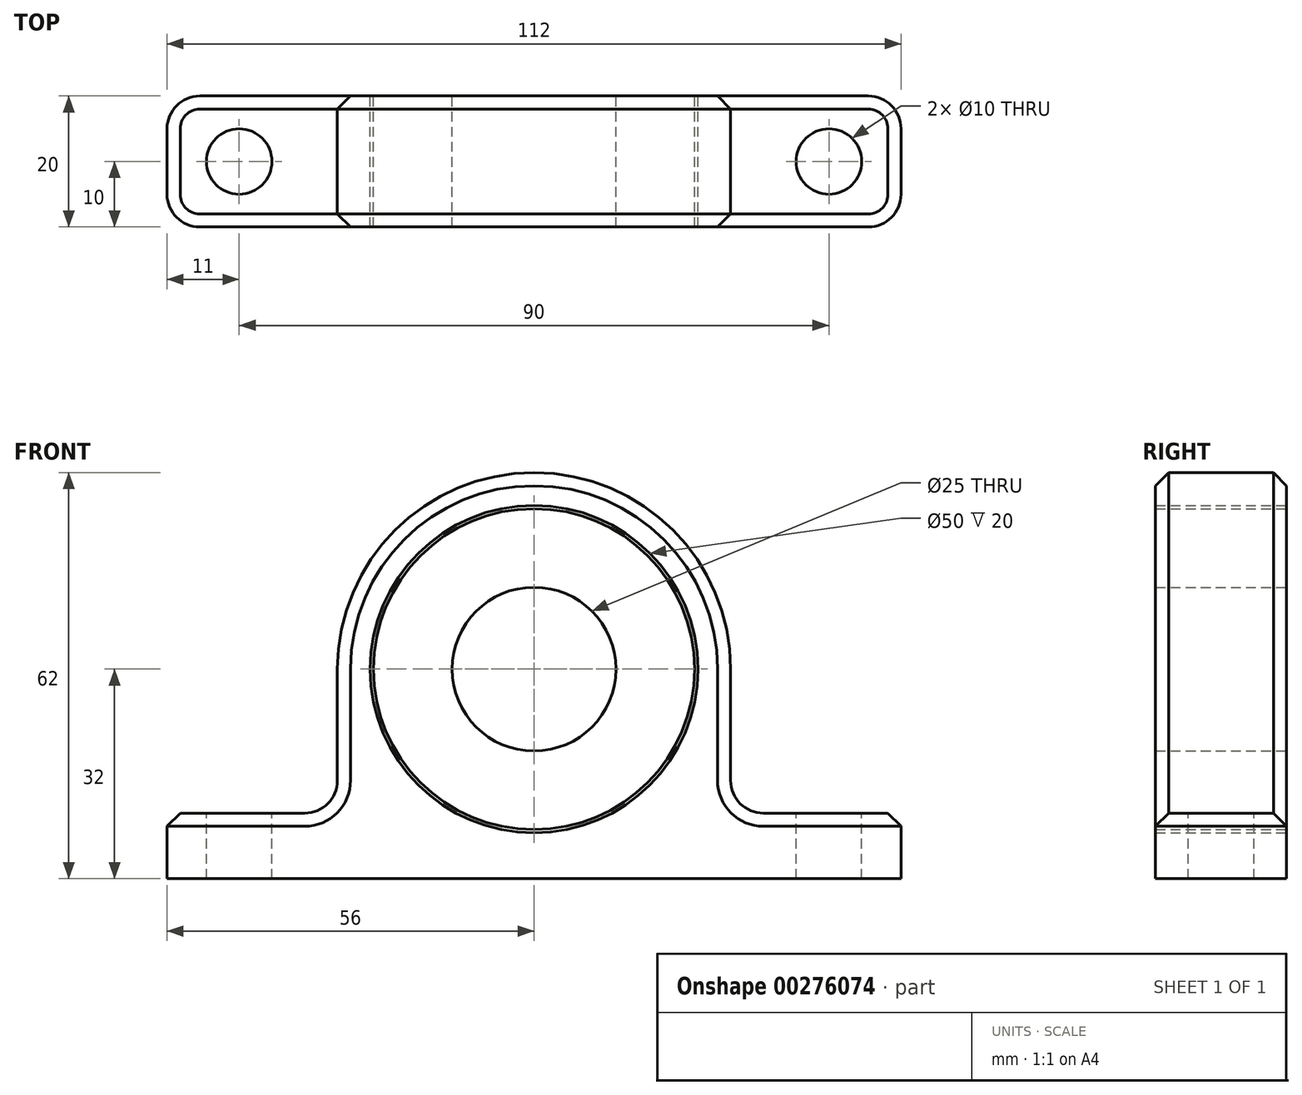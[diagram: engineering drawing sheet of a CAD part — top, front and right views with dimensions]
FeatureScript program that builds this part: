
annotation { "Feature Type Name" : "Feature", "Feature Type Description" : "" }
export const myFeature = defineFeature(function(context is Context, id is Id, definition is map)
    precondition{}
    {
        {
            var Q0;
            Q0=qCreatedBy(makeId("Front.planeOp"),FACE);
            var sketch = newSketch(context, id + "F0", { "sketchPlane" : qUnion([Q0])});
            skCircle(sketch, "E0", {"center": v(0, 32) * mm, "radius": 12.5 * mm});
            skLineSegment(sketch, "E1.bottom", {"start": v(-56, 0) * mm, "end": v(56, 0) * mm});
            skLineSegment(sketch, "E1.top", {"start": v(35, 10) * mm, "end": v(56, 10) * mm});
            skLineSegment(sketch, "E1.left", {"start": v(-56, 0) * mm, "end": v(-56, 10) * mm});
            skLineSegment(sketch, "E1.right", {"start": v(56, 0) * mm, "end": v(56, 10) * mm});
            skCircle(sketch, "E2", {"center": v(0, 32) * mm, "radius": 30 * mm});
            skCircle(sketch, "E3", {"center": v(0, 32) * mm, "radius": 25 * mm});
            skLineSegment(sketch, "E4", {"start": v(30, 32) * mm, "end": v(30, 15) * mm});
            skLineSegment(sketch, "E5", {"start": v(-30, 32) * mm, "end": v(-30, 15) * mm});
            skArc(sketch, "E6.filletArc", {"start": v(30, 15) * mm, "mid": v(31.46, 11.46) * mm, "end": v(35, 10) * mm});
            skLineSegment(sketch, "E7", {"start": v(-56, 10) * mm, "end": v(-35, 10) * mm});
            skArc(sketch, "E8.filletArc", {"start": v(-35, 10) * mm, "mid": v(-31.46, 11.46) * mm, "end": v(-30, 15) * mm});
            skCircle(sketch, "E9", {"center": v(0, 32) * mm, "radius": 24.5 * mm});
            skSolve(sketch);
        }
        {
            var Q0;
            Q0=makeQuery(id+"F0.imprint","IMPRINT",FACE,{"disambiguationData":[TD([[makeQuery(id+"F0.imprint","IMPRINT",EDGE,{"derivedFrom":sQuery(id+"F0.wireOp",EDGE,"E1.bottom")}),1.0]])]});
            var Q1;
            Q1=makeQuery(id+"F0.imprint","IMPRINT",FACE,{"disambiguationData":[TD([[makeQuery(id+"F0.imprint","IMPRINT",EDGE,{"derivedFrom":sQuery(id+"F0.wireOp",EDGE,"E3")}),-1.0]])]});
            var Q2;
            Q2=makeQuery(id+"F0.imprint","IMPRINT",FACE,{"disambiguationData":[TD([[makeQuery(id+"F0.imprint","IMPRINT",EDGE,{"derivedFrom":sQuery(id+"F0.wireOp",EDGE,"E0")}),-1.0]])]});
            extrude(context, id + "F1", {"entities" : qUnion([Q0, Q1, Q2]), "endBound" : BoundingType.SYMMETRIC, "depth" : 20 * mm});
        }
        {
            var Q0;
            Q0=makeQuery(id+"F1.opExtrude","CAP_EDGE",EDGE,{"disambiguationData":[OSD([sQuery(id+"F0.wireOp",EDGE,"E1.left")])],"isStart":false});
            var Q1;
            Q1=makeQuery(id+"F1.opExtrude","CAP_EDGE",EDGE,{"disambiguationData":[OSD([sQuery(id+"F0.wireOp",EDGE,"E1.right")])],"isStart":false});
            var Q2;
            Q2=makeQuery(id+"F1.opExtrude","CAP_EDGE",EDGE,{"disambiguationData":[OSD([sQuery(id+"F0.wireOp",EDGE,"E1.right")])],"isStart":true});
            var Q3;
            Q3=makeQuery(id+"F1.opExtrude","CAP_EDGE",EDGE,{"disambiguationData":[OSD([sQuery(id+"F0.wireOp",EDGE,"E1.left")])],"isStart":true});
            fillet(context, id + "F2", {"entities" : qUnion([Q0, Q1, Q2, Q3]), "radius" : 5 * mm, "tangentPropagation" : true, "allowEdgeOverflow" : false});
        }
        {
            var Q0;
            Q0=makeQuery(id+"F1.opExtrude","SWEPT_FACE",FACE,{"disambiguationData":[OSD([sQuery(id+"F0.wireOp",EDGE,"E1.top")])]});
            var sketch = newSketch(context, id + "F3", { "sketchPlane" : qUnion([Q0])});
            skCircle(sketch, "E10", {"center": v(-45, 0) * mm, "radius": 5 * mm});
            skCircle(sketch, "E11", {"center": v(45, 0) * mm, "radius": 5 * mm});
            skSolve(sketch);
        }
        {
            var Q0;
            Q0=makeQuery(id+"F3.imprint","IMPRINT",FACE,{"disambiguationData":[TD([[makeQuery(id+"F3.imprint","IMPRINT",EDGE,{"derivedFrom":sQuery(id+"F3.wireOp",EDGE,"E10")}),1.0]])]});
            var Q1;
            Q1=makeQuery(id+"F3.imprint","IMPRINT",FACE,{"disambiguationData":[TD([[makeQuery(id+"F3.imprint","IMPRINT",EDGE,{"derivedFrom":sQuery(id+"F3.wireOp",EDGE,"E11")}),1.0]])]});
            extrude(context, id + "F4", {"entities" : qUnion([Q0, Q1]), "operationType" : NewBodyOperationType.REMOVE, "oppositeDirection" : true, "depth" : 10 * mm});
        }
        {
            var Q0;
            Q0=makeQuery(id+"F1.opExtrude","CAP_EDGE",EDGE,{"disambiguationData":[OSD([sQuery(id+"F0.wireOp",EDGE,"E2")])],"isStart":false});
            var Q1;
            Q1=makeQuery(id+"F1.opExtrude","CAP_EDGE",EDGE,{"disambiguationData":[OSD([sQuery(id+"F0.wireOp",EDGE,"E4")])],"isStart":false});
            var Q2;
            Q2=makeQuery(id+"F1.opExtrude","CAP_EDGE",EDGE,{"disambiguationData":[OSD([sQuery(id+"F0.wireOp",EDGE,"E4")])],"isStart":true});
            var Q3;
            Q3=makeQuery(id+"F1.opExtrude","CAP_EDGE",EDGE,{"disambiguationData":[OSD([sQuery(id+"F0.wireOp",EDGE,"E2")])],"isStart":true});
            var Q4;
            Q4=makeQuery(id+"F1.opExtrude","CAP_EDGE",EDGE,{"disambiguationData":[OSD([sQuery(id+"F0.wireOp",EDGE,"E5")])],"isStart":false});
            var Q5;
            Q5=makeQuery(id+"F1.opExtrude","CAP_EDGE",EDGE,{"disambiguationData":[OSD([sQuery(id+"F0.wireOp",EDGE,"E5")])],"isStart":true});
            chamfer(context, id + "F5", {"entities" : qUnion([Q0, Q1, Q2, Q3, Q4, Q5]), "width" : 2 * mm, "tangentPropagation" : true});
        }
    });
